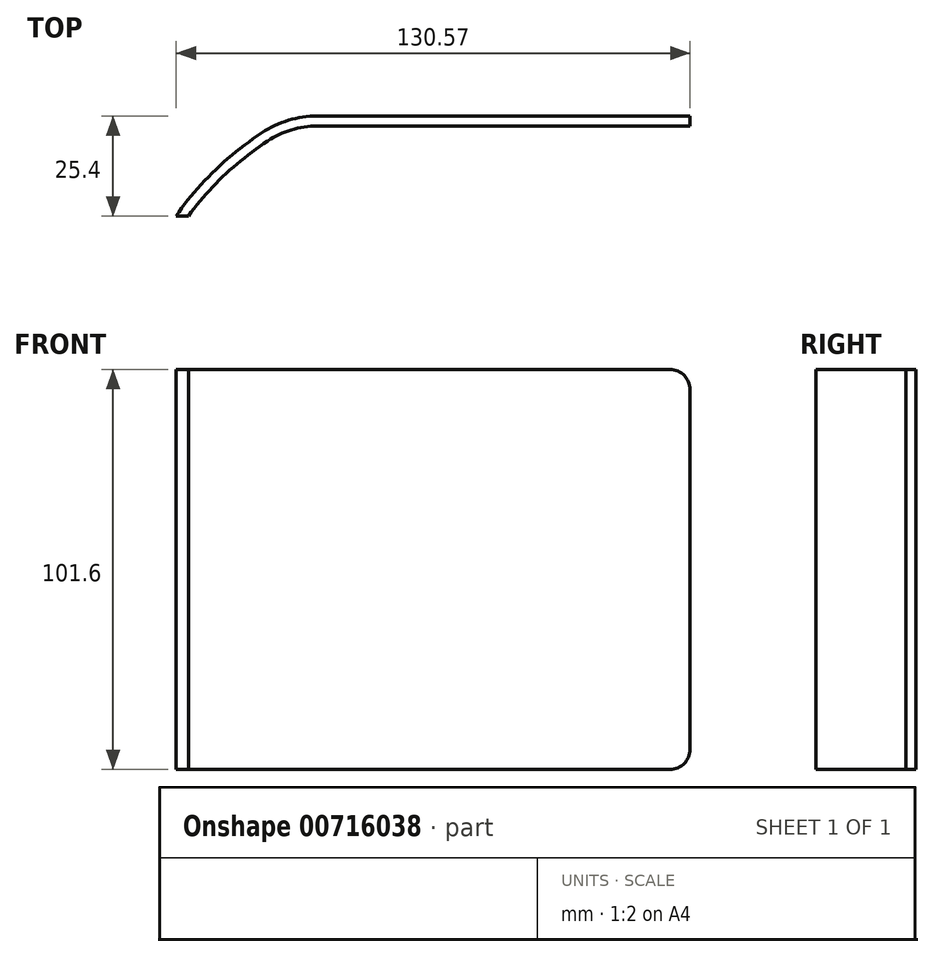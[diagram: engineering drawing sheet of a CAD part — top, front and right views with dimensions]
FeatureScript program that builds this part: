
annotation { "Feature Type Name" : "Feature", "Feature Type Description" : "" }
export const myFeature = defineFeature(function(context is Context, id is Id, definition is map)
    precondition{}
    {
        {
            var Q0;
            Q0=qCreatedBy(makeId("Front.planeOp"),FACE);
            var sketch = newSketch(context, id + "F0", { "sketchPlane" : qUnion([Q0])});
            skLineSegment(sketch, "E0.bottom", {"start": v(-49.59, 42.25) * mm, "end": v(52.01, 42.25) * mm});
            skLineSegment(sketch, "E0.top", {"start": v(-49.59, -59.35) * mm, "end": v(52.01, -59.35) * mm});
            skLineSegment(sketch, "E0.left", {"start": v(-49.59, 42.25) * mm, "end": v(-49.59, -59.35) * mm});
            skLineSegment(sketch, "E0.right", {"start": v(52.01, 42.25) * mm, "end": v(52.01, -59.35) * mm});
            skLineSegment(sketch, "E1.left", {"start": v(-49.59, 42.25) * mm, "end": v(-49.59, 42.25) * mm});
            skLineSegment(sketch, "E2.bottom", {"start": v(-49.59, 42.25) * mm, "end": v(-87.69, 42.25) * mm});
            skLineSegment(sketch, "E2.top", {"start": v(-49.59, -59.35) * mm, "end": v(-87.69, -59.35) * mm});
            skLineSegment(sketch, "E2.right", {"start": v(-87.69, 42.25) * mm, "end": v(-87.69, -59.35) * mm});
            skLineSegment(sketch, "E3", {"start": v(52.01, -8.55) * mm, "end": v(-49.59, -8.55) * mm, "construction": true});
            skLineSegment(sketch, "E4.bottom", {"start": v(52.01, 42.25) * mm, "end": v(12.64, 42.25) * mm, "construction": true});
            skLineSegment(sketch, "E4.top", {"start": v(52.01, 27) * mm, "end": v(12.64, 27) * mm, "construction": true});
            skLineSegment(sketch, "E4.left", {"start": v(52.01, 42.25) * mm, "end": v(52.01, 27) * mm, "construction": true});
            skLineSegment(sketch, "E4.right", {"start": v(12.64, 42.25) * mm, "end": v(12.64, 27) * mm, "construction": true});
            skSolve(sketch);
        }
        {
            var Q0;
            Q0=makeQuery(id+"F0.imprint","IMPRINT",FACE,{"disambiguationData":[TD([[makeQuery(id+"F0.imprint","IMPRINT",EDGE,{"derivedFrom":sQuery(id+"F0.wireOp",EDGE,"E0.bottom")}),-1.0]])]});
            extrude(context, id + "F1", {"entities" : qUnion([Q0]), "endBound" : BoundingType.SYMMETRIC, "depth" : 25.4 * mm, "offsetDistance" : 25.4 * mm});
        }
        {
            var Q0;
            Q0=makeQuery(id+"F1.opExtrude","SWEPT_FACE",FACE,{"disambiguationData":[OSD([sQuery(id+"F0.wireOp",EDGE,"E0.bottom")])]});
            var sketch = newSketch(context, id + "F2", { "sketchPlane" : qUnion([Q0])});
            skEllipse(sketch, "E5", {"center": v(-49.59, -12.7) * mm, "majorRadius": 42.74 * mm, "minorRadius": 21.35 * mm, "majorAxis": v(0.78, 0.63)});
            skLineSegment(sketch, "E6", {"start": v(-49.59, -12.7) * mm, "end": v(-78.56, -12.7) * mm});
            skLineSegment(sketch, "E7", {"start": v(-49.59, -12.7) * mm, "end": v(-49.59, 12.7) * mm});
            skSolve(sketch);
        }
        {
            var Q0;
            {var subQ2=sQuery(id+"F2.wireOp",EDGE,"E6");Q0=makeQuery(id+"F2.imprint","IMPRINT",FACE,{"disambiguationData":[TD([[makeQuery(id+"F2.imprint","IMPRINT",EDGE,{"derivedFrom":subQ2}),-1.0]])]});}
            extrude(context, id + "F3", {"entities" : qUnion([Q0]), "operationType" : NewBodyOperationType.ADD, "oppositeDirection" : true, "depth" : 101.6 * mm, "offsetDistance" : 25.4 * mm});
        }
        {
            var Q0;
            Q0=makeQuery(id+"F3.boolean.opBoolean","MERGE",EDGE,{"derivedFrom":[makeQuery(id+"F1.opExtrude","CAP_EDGE",EDGE,{"disambiguationData":[OSD([sQuery(id+"F0.wireOp",EDGE,"E0.left")])],"isStart":true}),makeQuery(id+"F3.opExtrude","SWEPT_EDGE",EDGE,{"disambiguationData":[OSD([sQuery(id+"F0.wireOp",EDGE,"E0.bottom"),sQuery(id+"F2.wireOp",EDGE,"E5"),sQuery(id+"F2.wireOp",EDGE,"E7")])]})]});
            fillet(context, id + "F4", {"entities" : qUnion([Q0]), "radius" : 25.4 * mm, "tangentPropagation" : true, "allowEdgeOverflow" : false});
        }
        {
            var Q0;
            Q0=makeQuery(id+"F3.boolean.opBoolean","MERGE",FACE,{"derivedFrom":[makeQuery(id+"F1.opExtrude","SWEPT_FACE",FACE,{"disambiguationData":[OSD([sQuery(id+"F0.wireOp",EDGE,"E0.bottom")])]}),makeQuery(id+"F3.opExtrude","CAP_FACE",FACE,{"disambiguationData":[OSD([sQuery(id+"F2.wireOp",EDGE,"E5"),sQuery(id+"F2.wireOp",EDGE,"E6"),sQuery(id+"F2.wireOp",EDGE,"E7")])],"isStart":true})]});
            var Q1;
            Q1=makeQuery(id+"F3.boolean.opBoolean","MERGE",FACE,{"derivedFrom":[makeQuery(id+"F1.opExtrude","CAP_FACE",FACE,{"disambiguationData":[OSD([sQuery(id+"F0.wireOp",EDGE,"E0.bottom"),sQuery(id+"F0.wireOp",EDGE,"E0.top"),sQuery(id+"F0.wireOp",EDGE,"E0.right"),sQuery(id+"F0.wireOp",EDGE,"E0.left")])],"isStart":false}),makeQuery(id+"F3.opExtrude","SWEPT_FACE",FACE,{"disambiguationData":[OSD([sQuery(id+"F2.wireOp",EDGE,"E6")])]})]});
            var Q2;
            Q2=makeQuery(id+"F1.opExtrude","SWEPT_FACE",FACE,{"disambiguationData":[OSD([sQuery(id+"F0.wireOp",EDGE,"E0.right")])]});
            var Q3;
            Q3=makeQuery(id+"F3.boolean.opBoolean","MERGE",FACE,{"derivedFrom":[makeQuery(id+"F1.opExtrude","SWEPT_FACE",FACE,{"disambiguationData":[OSD([sQuery(id+"F0.wireOp",EDGE,"E0.top")])]}),makeQuery(id+"F3.opExtrude","CAP_FACE",FACE,{"disambiguationData":[OSD([sQuery(id+"F2.wireOp",EDGE,"E5"),sQuery(id+"F2.wireOp",EDGE,"E6"),sQuery(id+"F2.wireOp",EDGE,"E7")])],"isStart":false})]});
            shell(context, id + "F5", {"entities" : qUnion([Q0, Q1, Q2, Q3]), "thickness" : 2.54 * mm});
        }
        {
            var Q0;
            Q0=makeQuery(id+"F3.opExtrude","SWEPT_FACE",FACE,{"disambiguationData":[OSD([sQuery(id+"F2.wireOp",EDGE,"E5")])]});
            var Q1;
            Q1=makeQuery(id+"F4.opFillet","BLEND_FACE",FACE,{"disambiguationData":[OSD([sQuery(id+"F0.wireOp",EDGE,"E0.bottom"),sQuery(id+"F0.wireOp",EDGE,"E0.left"),sQuery(id+"F2.wireOp",EDGE,"E5"),sQuery(id+"F2.wireOp",EDGE,"E7")])]});
            var Q2;
            Q2=makeQuery(id+"F1.opExtrude","CAP_FACE",FACE,{"disambiguationData":[OSD([sQuery(id+"F0.wireOp",EDGE,"E0.bottom"),sQuery(id+"F0.wireOp",EDGE,"E0.top"),sQuery(id+"F0.wireOp",EDGE,"E0.right"),sQuery(id+"F0.wireOp",EDGE,"E0.left")])],"isStart":true});
            var Q3;
            Q3=makeQuery(id+"F1.opExtrude","SWEPT_BODY",BODY,{"disambiguationData":[OSD([sQuery(id+"F0.wireOp",EDGE,"E0.bottom"),sQuery(id+"F0.wireOp",EDGE,"E0.top"),sQuery(id+"F0.wireOp",EDGE,"E0.right"),sQuery(id+"F0.wireOp",EDGE,"E0.left")])]});
            shell(context, id + "F7", {"entities" : qUnion([Q0, Q1, Q2]), "parts" : qUnion([Q3]), "thickness" : 2.54 * mm});
        }
        {
            var Q0;
            Q0=makeQuery(id+"F1.opExtrude","SWEPT_EDGE",EDGE,{"disambiguationData":[OSD([sQuery(id+"F0.wireOp",EDGE,"E0.top"),sQuery(id+"F0.wireOp",EDGE,"E0.right")])]});
            var Q1;
            Q1=makeQuery(id+"F1.opExtrude","SWEPT_EDGE",EDGE,{"disambiguationData":[OSD([sQuery(id+"F0.wireOp",EDGE,"E0.bottom"),sQuery(id+"F0.wireOp",EDGE,"E0.right")])]});
            fillet(context, id + "F8", {"entities" : qUnion([Q0, Q1]), "radius" : 5.08 * mm, "tangentPropagation" : true, "allowEdgeOverflow" : false});
        }
    });
